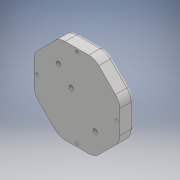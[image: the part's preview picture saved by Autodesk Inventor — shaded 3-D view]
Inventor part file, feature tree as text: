
AUTODESK INVENTOR PART (.ipt)
format: ipt  version: 2018 (Build 220112000, 112)  size: 270,848 bytes
history: native  units: mm
features: sketch x8, extrude x3, hole x3, pattern_circular x2, loft x1, chamfer x1, fillet x1
ambient origin geometry x8: Origin, YZ Plane, XZ Plane, XY Plane, X Axis, Y Axis, Z Axis, Center Point
bodies: Body1 (feature_tree)
feature tree (19):
  extrude  "Extrusion3"  Depth=10.0mm
  loft  "Loft2"
  pattern_circular  "Circular Pattern1"  Count=4 Angle=360.0deg
  extrude  "Extrusion4"  Depth=10.0mm TaperAngle=0.0deg
  hole  "Hole1"  [1 undecoded]
  chamfer  "Chamfer1"  Distance=10.0mm
  fillet  "Fillet3"  Radius=9.0mm
  hole  "Hole2"  [1 undecoded]
  pattern_circular  "Circular Pattern2"  Count=2  [1 undecoded]
  extrude  "Extrusion6"  Depth=1.0mm
  hole  "Hole3"  [1 undecoded]
  sketch  "Sketch5"  dims[d9=10.0mm d10=0.0mm d11=1.8mm]
  sketch  "Sketch6"  dims[d19=60.0mm d20=12.0mm]
  sketch  "Sketch8"  dims[d21=1.8mm]
  sketch  "Sketch9"  dims[d22=12.0mm]
  sketch  "Sketch10"  dims[d23=0.0mm d24=90.0deg]
  sketch  "Sketch12"  dims[d25=0.0mm d26=90.0deg d27=40.0mm d28=360.0deg]
  sketch  "Sketch14"  dims[d30=5.0mm d31=10.0mm d32=0.0mm]
  sketch  "Sketch15"  dims[d33=1.8mm d34=6.0mm d35=4.0mm d36=2.0mm d37=90.0deg d38=15.0mm d39=20.594885mm d44=5.0mm d45=2.0mm d46=45.0deg d48=10.0mm d49=2.0mm d50=4.0mm d51=9.0mm d52=3.0mm d53=6.0mm d54=5.0mm d55=1.0mm d56=90.0deg d57=15.0mm d58=0.0mm d59=20.0mm d60=360.0deg d62=20.0mm d63=1.0mm d64=1.0mm d65=10.0mm d66=0.0mm d67=45.0deg d68=4.0mm d69=3.0mm d70=6.0mm d71=8.0mm d72=10.0mm d73=90.0deg d74=8.0mm d75=20.594885mm]
note: 4 required parameter values undecoded (feature->parameter linkage not recoverable at this tier; creation-order binding heuristic only, values carry confidence <= 0.55)
